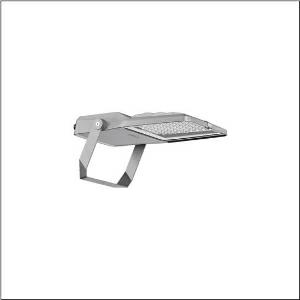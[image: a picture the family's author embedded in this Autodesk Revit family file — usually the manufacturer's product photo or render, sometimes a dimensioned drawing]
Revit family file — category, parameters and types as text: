
# Revit family: floodlight_fl_21_iq_mini___pl64_5xa7772c1e1a_659a
name_source: partatom
category: Lighting Fixtures
units: mm (PartAtom-declared; Revit-internal decimal feet)

## family parameters
Cut with Voids When Loaded = No
Host = Face
Light Source = No
Part Type = Normal
Room Calculation Point = No
Round Connector Dimension = Use Diameter
Shared = No

## types (1)
- --- (1 x LED, 9770 lm, 87.2 W, 2200K)
    Apparent Load = 87 VA
    CIE Flux Codes = 28 80 98 100 100
    Color Rendering = 70
    Color Temperature = 2200K
    Default Elevation = 1800 mm
    Description = Floodlight FL 21 iQ mini, floodlight, primary light control with lens, of PMMA, primary optical cover: protective disc, of toughened safety glass, transparent, light distribution: PL64, light emission: direct distribution, installation type: surface-mounted, LED, High Power LED, rated luminous flux: 9.770lm, luminous efficacy: 112lm/W, light colour: 722, colour temperature: 2200K, control gear: iQ Street-Remote/DALI, control: Street-Remote, Auto-Match, Temp-Guard, Night-Set, Smart-Wire, Desk-Remote (wireless, voltage-free reading and setting of iQ features in the workshop via application-optimized NFC function/RFID function), optimised constant luminous flux control (CLO 2.0), with terminal, 6-pole, mains connection: 220..240V, AC, 50/60Hz, start of lifetime: 87W, end of service life: 92W, reduction: 40W, luminaire housing, of diecast aluminium, powder-coated, Siteco® metallic grey (DB 702S), corrosivity category C5 mid according to DIN EN ISO 12944, suitable for swimming pools, chlorine-resistant, sealing non-destructively replaceable, mounting bracket, of steel, galvanised, powder-coated, Siteco® metallic grey (DB 702S), protection rating (complete): IP66, insulation class (complete): insulation class II (safety insulation), certification: CE, ENEC, VDE, protection symbol: D, impact resistance: IK08, permissible operating ambient temperature: -40..+40°C, permissible operating ambient temperature for outdoor applications: -40..+50°C, standard: DIN EN 12944, LABS conformity tested according to VDMA 24364:2018-05, packaging unit: 1 piece

Light Distribution: PL64
    Height = 70 mm
    Lamp = 1 x LED
    Lamp Light Flux = 9770 lm
    Lamp Power = 87.2 W
    Lamp count = 1
    Length = 485 mm
    Luminous efficacy = 112 lm/W
    Manufacturer = Siteco
    ModVariant = No
    Model = 5XA7772C1E1A
    Number of Poles = 1
    OnlyDefault = Yes
    Power Factor = 1
    Product Name = Floodlight FL 21 iQ mini | PL64
    Product group = floodlight | pylon annexe
    ProductGroupID = 6200
    Protection Class = Protection class II
    Protection Degree = IP 66
    RLX_Detail_Level = 1
    RLX_Emergency_Light_Flux = 0 lm
    RLX_Emergency_Type = 0
    RLX_Emergency_Type_DB = No
    RlxData = <blob elided: 96133 chars, md5=33660059>
    Socket = socket
    Standby Power = 0 W
    System Light Flux = 9770 lm
    System Power = 87 W
    Type Comments = factory setting: luminous flux: 100 % | dim-lin: 254 | 456 mA
    Type Image = l_1006845.jpg
    URL = http://relux.com
    VarID = @adj_166470
    Voltage = 0 V
    Weight = 0.00 kg
    Width = 337 mm

## geometry (parser evidence)
native form markers: Blend x4, Sweep x15
no freeform markers — native parametric forms only
